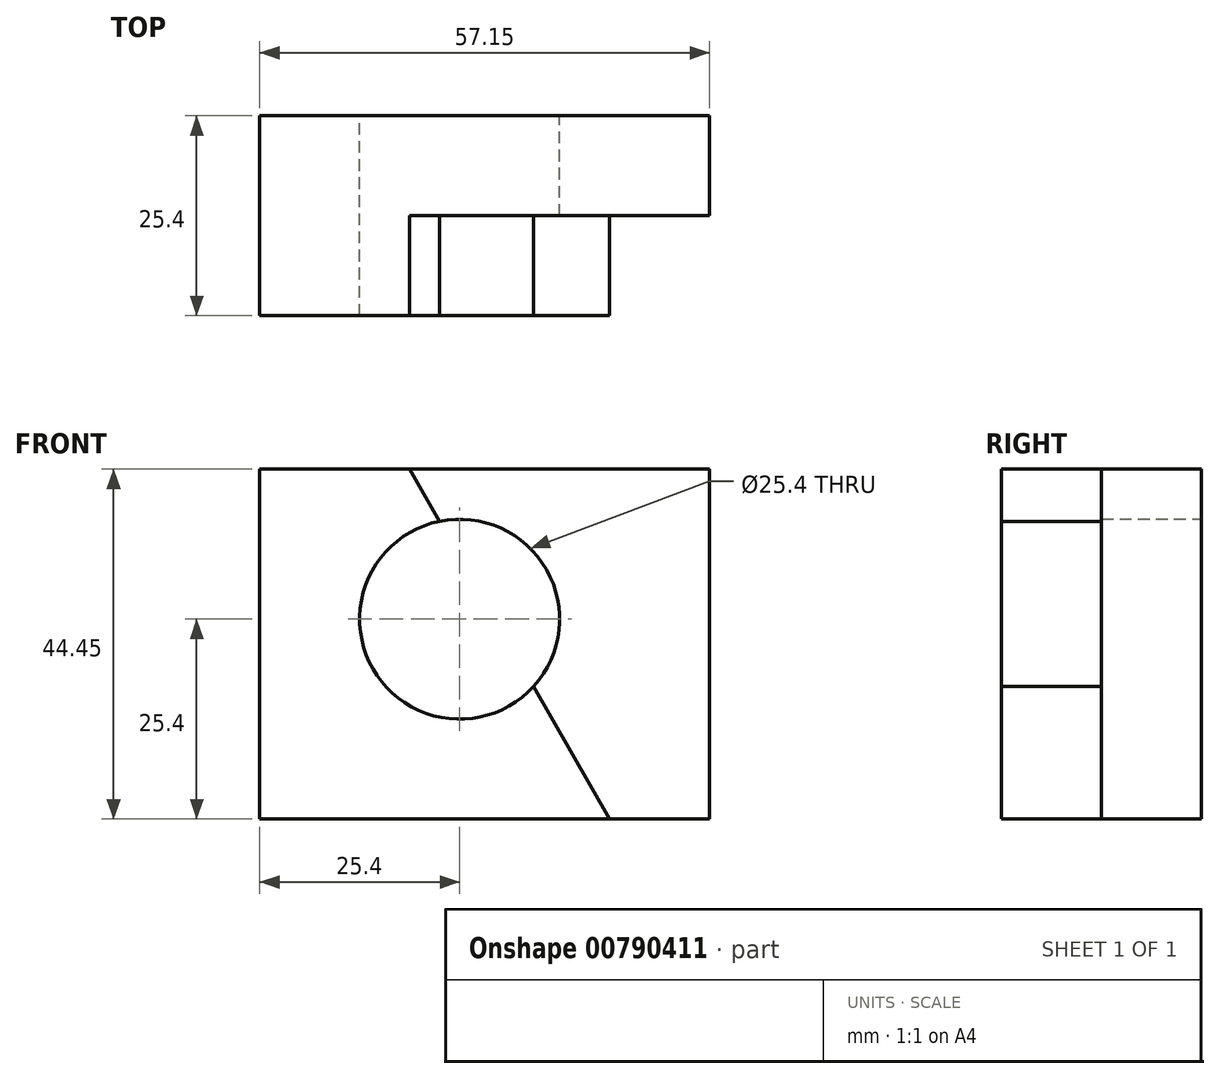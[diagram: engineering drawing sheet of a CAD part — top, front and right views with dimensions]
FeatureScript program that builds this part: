
annotation { "Feature Type Name" : "Feature", "Feature Type Description" : "" }
export const myFeature = defineFeature(function(context is Context, id is Id, definition is map)
    precondition{}
    {
        {
            var Q0;
            Q0=qCreatedBy(makeId("Front.planeOp"),FACE);
            var sketch = newSketch(context, id + "F0", { "sketchPlane" : qUnion([Q0])});
            skLineSegment(sketch, "E0.bottom", {"start": v(0, 0) * mm, "end": v(57.15, 0) * mm});
            skLineSegment(sketch, "E0.top", {"start": v(0, 44.45) * mm, "end": v(57.15, 44.45) * mm});
            skLineSegment(sketch, "E0.left", {"start": v(0, 0) * mm, "end": v(0, 44.45) * mm});
            skLineSegment(sketch, "E0.right", {"start": v(57.15, 0) * mm, "end": v(57.15, 44.45) * mm});
            skCircle(sketch, "E1", {"center": v(25.4, 25.4) * mm, "radius": 12.7 * mm});
            skSolve(sketch);
        }
        {
            var Q0;
            Q0=makeQuery(id+"F0.imprint","IMPRINT",FACE,{"disambiguationData":[TD([[makeQuery(id+"F0.imprint","IMPRINT",EDGE,{"derivedFrom":sQuery(id+"F0.wireOp",EDGE,"E0.bottom")}),1.0]])]});
            extrude(context, id + "F1", {"entities" : qUnion([Q0]), "depth" : 25.4 * mm, "offsetDistance" : 25.4 * mm});
        }
        {
            var Q0;
            Q0=makeQuery(id+"F1.opExtrude","CAP_FACE",FACE,{"disambiguationData":[OSD([sQuery(id+"F0.wireOp",EDGE,"E0.bottom"),sQuery(id+"F0.wireOp",EDGE,"E0.top"),sQuery(id+"F0.wireOp",EDGE,"E0.left"),sQuery(id+"F0.wireOp",EDGE,"E0.right"),sQuery(id+"F0.wireOp",EDGE,"E1")])],"isStart":false});
            var sketch = newSketch(context, id + "F2", { "sketchPlane" : qUnion([Q0])});
            skLineSegment(sketch, "E2", {"start": v(19.05, 44.45) * mm, "end": v(22.83, 37.84) * mm});
            skLineSegment(sketch, "E3", {"start": v(19.05, 44.45) * mm, "end": v(57.15, 44.45) * mm});
            skLineSegment(sketch, "E4", {"start": v(57.15, 44.45) * mm, "end": v(57.15, 0) * mm});
            skLineSegment(sketch, "E5", {"start": v(57.15, 0) * mm, "end": v(44.45, 0) * mm});
            skArc(sketch, "E6", {"start": v(34.8, 16.87) * mm, "mid": v(36.43, 31.7) * mm, "end": v(22.83, 37.84) * mm});
            skLineSegment(sketch, "E7.trimOffspring", {"start": v(34.8, 16.87) * mm, "end": v(44.45, 0) * mm});
            skSolve(sketch);
        }
        {
            var Q0;
            Q0=qSketchRegion(id+"F2",true);
            extrude(context, id + "F3", {"entities" : qUnion([Q0]), "operationType" : NewBodyOperationType.REMOVE, "oppositeDirection" : true, "depth" : 12.7 * mm, "offsetDistance" : 25.4 * mm});
        }
    });
